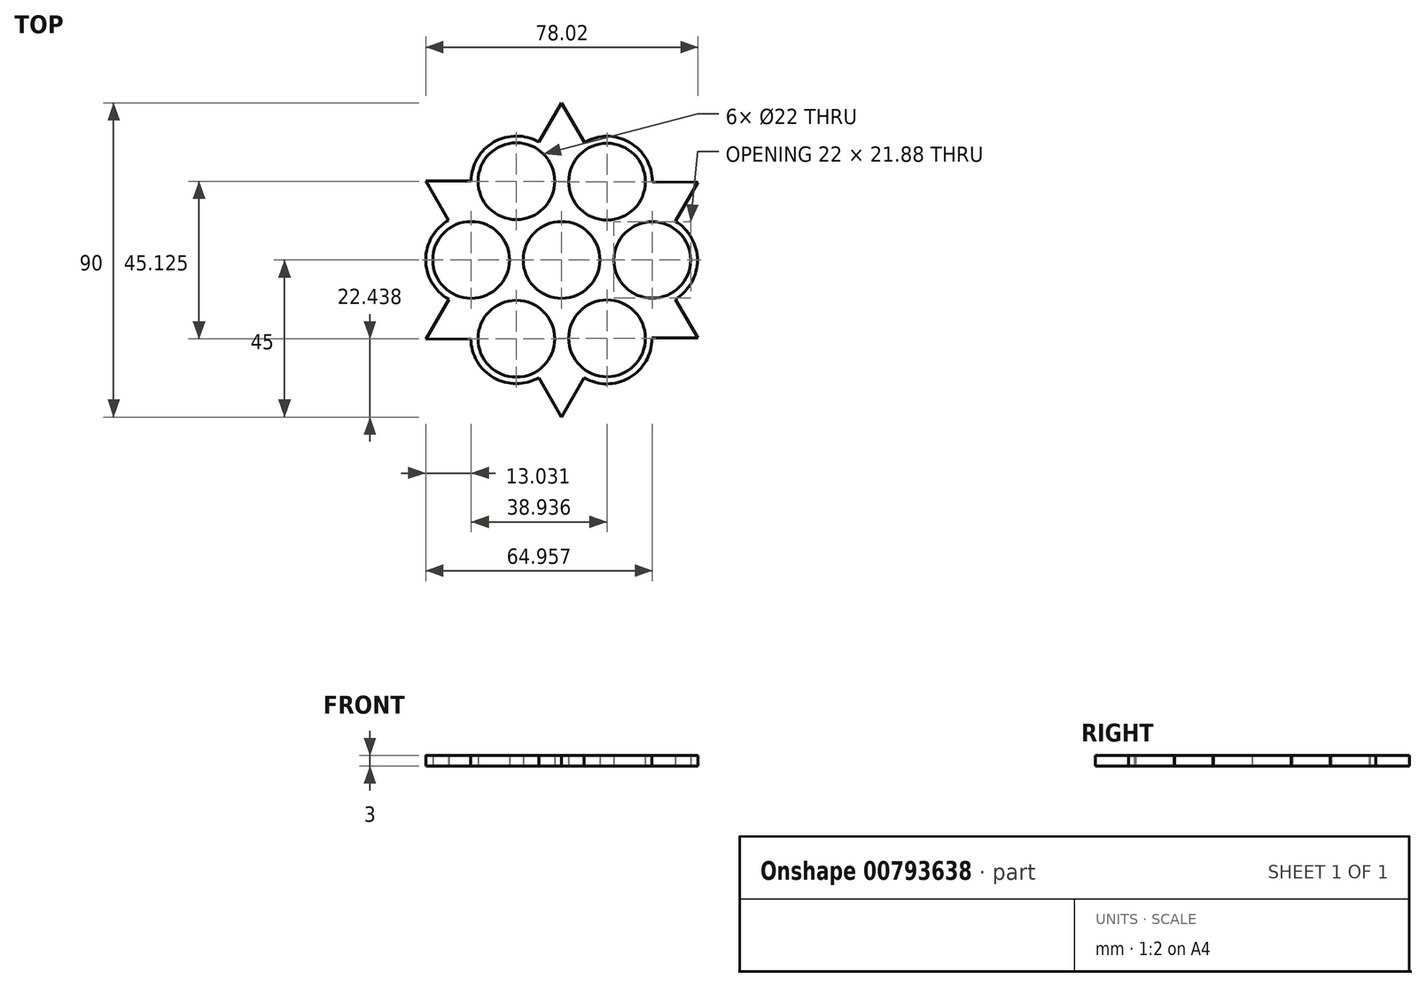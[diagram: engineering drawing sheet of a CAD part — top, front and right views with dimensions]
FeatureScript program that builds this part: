
annotation { "Feature Type Name" : "Feature", "Feature Type Description" : "" }
export const myFeature = defineFeature(function(context is Context, id is Id, definition is map)
    precondition{}
    {
        {
            var Q0;
            Q0=qCreatedBy(makeId("Top.planeOp"),FACE);
            var sketch = newSketch(context, id + "F0", { "sketchPlane" : qUnion([Q0])});
            skArc(sketch, "E0", {"start": v(11, 0) * mm, "mid": v(0, 11) * mm, "end": v(-11, 0) * mm});
            skLineSegment(sketch, "E1.2", {"start": v(0, 45) * mm, "end": v(6.53, 33.7) * mm});
            skLineSegment(sketch, "E2.0", {"start": v(39.08, 22.31) * mm, "end": v(32.55, 11.13) * mm});
            skLineSegment(sketch, "E2.2", {"start": v(-38.86, 22.69) * mm, "end": v(-25.92, 22.62) * mm});
            skLineSegment(sketch, "E3.2", {"start": v(-23.28, 0) * mm, "end": v(-23.35, 0.11) * mm});
            skLineSegment(sketch, "E4", {"start": v(-37, 0) * mm, "end": v(-36.9, 0) * mm});
            skLineSegment(sketch, "E5.trimOffspring", {"start": v(-25.98, 0) * mm, "end": v(-25.94, 0.06) * mm});
            skPoint(sketch, "E6.orphan", {"position": v(-38.97, -22.5) * mm});
            skLineSegment(sketch, "E7.trimOffspring", {"start": v(-25.9, 0) * mm, "end": v(-25.94, 0.06) * mm});
            skLineSegment(sketch, "E8.trimOffspring", {"start": v(26.03, 22.38) * mm, "end": v(39.08, 22.31) * mm});
            skLineSegment(sketch, "E9.trimOffspring", {"start": v(-6.47, 33.79) * mm, "end": v(0, 45) * mm});
            skLineSegment(sketch, "E10.trimOffspring", {"start": v(25.98, 0) * mm, "end": v(26.02, -0.06) * mm});
            skCircle(sketch, "E11", {"center": v(13.03, 22.44) * mm, "radius": 11 * mm});
            skCircle(sketch, "E12", {"center": v(-12.95, 22.56) * mm, "radius": 11 * mm});
            skArc(sketch, "E13", {"start": v(-14.9, 0) * mm, "mid": v(-25.9, 11) * mm, "end": v(-36.9, 0) * mm});
            skArc(sketch, "E14", {"start": v(37.02, -0.06) * mm, "mid": v(26.05, 10.94) * mm, "end": v(15.02, 0) * mm});
            skLineSegment(sketch, "E15", {"start": v(26.02, -0.06) * mm, "end": v(26.09, -0.06) * mm});
            skArc(sketch, "E16.MirrorCS", {"start": v(-14.9, 0) * mm, "mid": v(-25.9, -11) * mm, "end": v(-36.9, 0) * mm});
            skLineSegment(sketch, "E17.MirrorCS", {"start": v(-32.34, -11.26) * mm, "end": v(-38.86, -22.69) * mm});
            skLineSegment(sketch, "E18.MirrorCS", {"start": v(-38.86, -22.69) * mm, "end": v(-26.03, -22.63) * mm});
            skCircle(sketch, "E19.MirrorC", {"center": v(-12.95, -22.56) * mm, "radius": 11 * mm});
            skArc(sketch, "E20.MirrorCS", {"start": v(11, 0) * mm, "mid": v(0, -11) * mm, "end": v(-11, 0) * mm});
            skArc(sketch, "E21.MirrorCS", {"start": v(37.02, 0.06) * mm, "mid": v(26.05, -10.94) * mm, "end": v(15.02, 0) * mm});
            skLineSegment(sketch, "E22.MirrorCS", {"start": v(39.08, -22.31) * mm, "end": v(32.6, -11.23) * mm});
            skLineSegment(sketch, "E23.MirrorCS", {"start": v(25.92, -22.38) * mm, "end": v(39.08, -22.31) * mm});
            skCircle(sketch, "E24.MirrorC", {"center": v(13.03, -22.44) * mm, "radius": 11 * mm});
            skLineSegment(sketch, "E25.MirrorCS", {"start": v(0, -45) * mm, "end": v(6.47, -33.79) * mm});
            skLineSegment(sketch, "E26.MirrorCS", {"start": v(-6.53, -33.7) * mm, "end": v(0, -45) * mm});
            skLineSegment(sketch, "E27.trimOffspring", {"start": v(25.98, 0) * mm, "end": v(26.05, 0) * mm});
            skLineSegment(sketch, "E28.trimOffspring", {"start": v(26.09, -0.06) * mm, "end": v(26.02, 0.06) * mm});
            skLineSegment(sketch, "E29.trimOffspring", {"start": v(26.05, 0) * mm, "end": v(26.02, -0.06) * mm});
            skLineSegment(sketch, "E30.trimOffspring", {"start": v(26.09, -0.06) * mm, "end": v(26.05, 0) * mm});
            skPoint(sketch, "E31.MirrorCS.start.orphan", {"position": v(39.08, -22.31) * mm});
            skLineSegment(sketch, "E32.trimOffspring", {"start": v(-32.4, 11.35) * mm, "end": v(-38.86, 22.69) * mm});
            skArc(sketch, "E33", {"start": v(26.03, 22.38) * mm, "mid": v(19.55, 33.68) * mm, "end": v(6.53, 33.7) * mm});
            skArc(sketch, "E34.1.0", {"start": v(-6.36, 33.73) * mm, "mid": v(-19.4, 33.77) * mm, "end": v(-25.92, 22.5) * mm});
            skArc(sketch, "E34.2.0", {"start": v(-32.4, 11.35) * mm, "mid": v(-38.94, 0.1) * mm, "end": v(-32.44, -11.2) * mm});
            skArc(sketch, "E34.3.0", {"start": v(-26.03, -22.63) * mm, "mid": v(-19.44, -33.74) * mm, "end": v(-6.53, -33.7) * mm});
            skArc(sketch, "E34.4.0", {"start": v(6.36, -33.73) * mm, "mid": v(19.4, -33.77) * mm, "end": v(25.92, -22.5) * mm});
            skArc(sketch, "E34.5.0", {"start": v(32.6, -11.23) * mm, "mid": v(38.94, 0.03) * mm, "end": v(32.44, 11.2) * mm});
            skLineSegment(sketch, "E35", {"start": v(-32.44, -11.2) * mm, "end": v(-32.34, -11.26) * mm});
            skLineSegment(sketch, "E36", {"start": v(25.92, -22.5) * mm, "end": v(25.92, -22.38) * mm});
            skPoint(sketch, "E37.orphan", {"position": v(7.53, 31.96) * mm});
            skPoint(sketch, "E38.orphan", {"position": v(-26.03, -22.38) * mm});
            skPoint(sketch, "E39.orphan", {"position": v(32.4, -11.35) * mm});
            skSolve(sketch);
        }
        {
            var Q0;
            Q0 = qSketchRegion(id + "F0", true);
            extrude(context, id + "F1", {"entities" : qUnion([Q0]), "depth" : 3 * mm, "offsetDistance" : 25 * mm});
        }
    });
